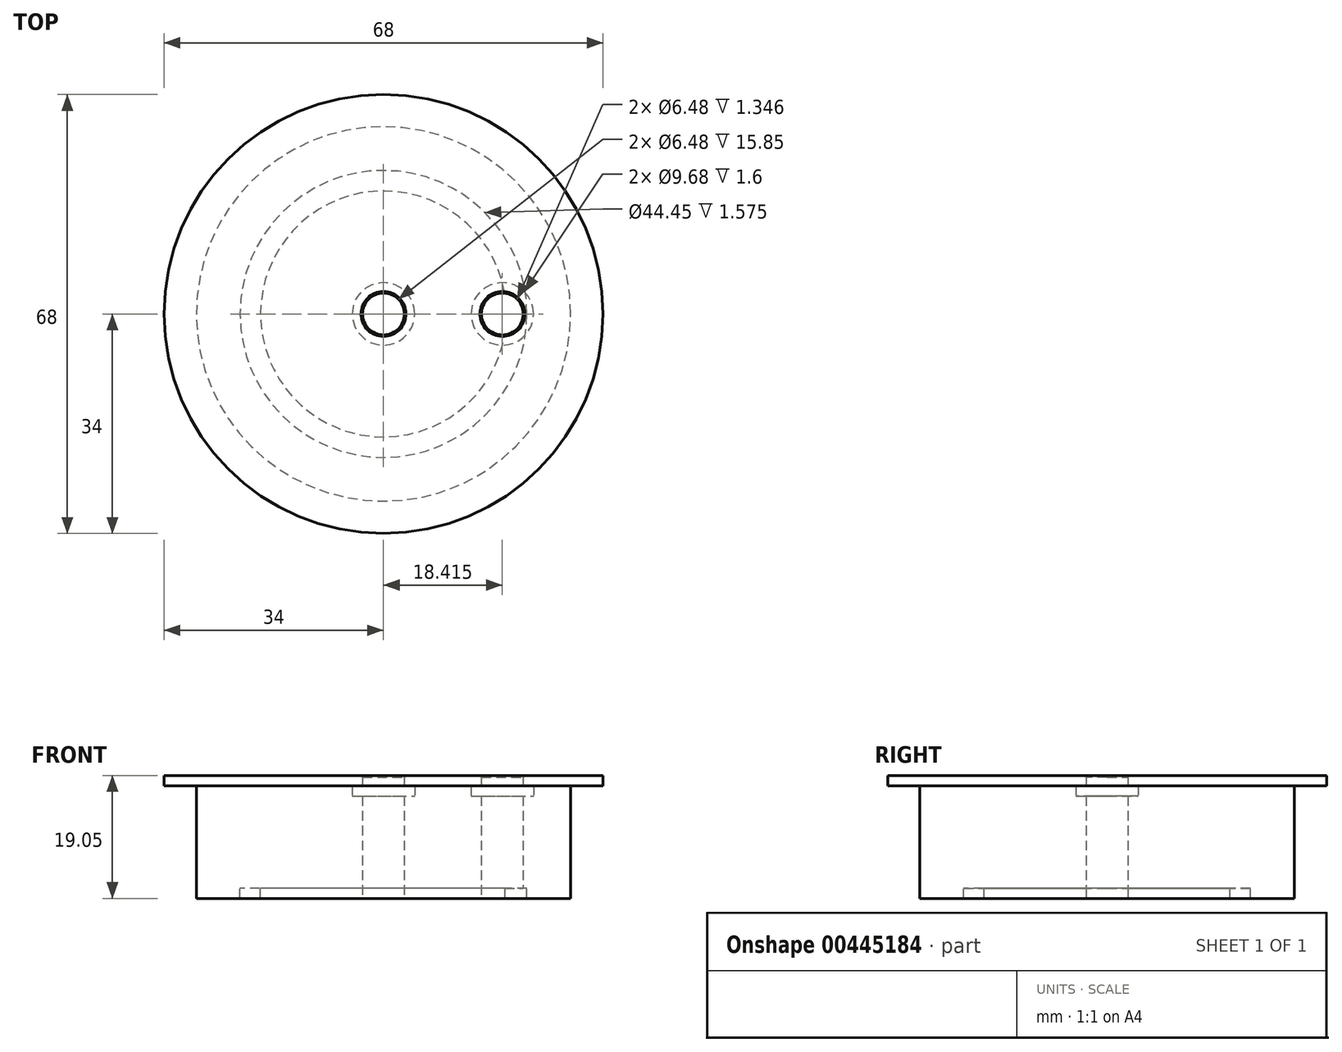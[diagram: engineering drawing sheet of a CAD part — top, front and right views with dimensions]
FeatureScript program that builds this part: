
annotation { "Feature Type Name" : "Feature", "Feature Type Description" : "" }
export const myFeature = defineFeature(function(context is Context, id is Id, definition is map)
    precondition{}
    {
        {
            var Q0;
            Q0=qCreatedBy(makeId("Front.planeOp"),FACE);
            var sketch = newSketch(context, id + "F0", { "sketchPlane" : qUnion([Q0])});
            skLineSegment(sketch, "E0", {"start": v(0, 0) * mm, "end": v(34, 0) * mm});
            skLineSegment(sketch, "E1", {"start": v(34, 0) * mm, "end": v(34, -1.6) * mm});
            skLineSegment(sketch, "E2", {"start": v(34, -1.6) * mm, "end": v(29, -1.6) * mm});
            skLineSegment(sketch, "E3", {"start": v(29, -1.6) * mm, "end": v(29, -19.05) * mm});
            skLineSegment(sketch, "E4", {"start": v(29, -19.05) * mm, "end": v(22.23, -19.05) * mm});
            skLineSegment(sketch, "E5", {"start": v(22.23, -19.05) * mm, "end": v(22.23, -17.48) * mm});
            skLineSegment(sketch, "E6", {"start": v(22.23, -17.48) * mm, "end": v(19.05, -17.48) * mm});
            skLineSegment(sketch, "E7", {"start": v(19.05, -17.48) * mm, "end": v(19.05, -19.05) * mm});
            skLineSegment(sketch, "E8", {"start": v(19.05, -19.05) * mm, "end": v(0, -19.05) * mm});
            skLineSegment(sketch, "E9", {"start": v(0, 0) * mm, "end": v(0, -19.05) * mm});
            skLineSegment(sketch, "E10", {"start": v(0, 18.94) * mm, "end": v(0, -33) * mm, "construction": true});
            skSolve(sketch);
        }
        {
            var Q0;
            Q0 = qSketchRegion(id + "F0", true);
            var Q1;
            Q1=sQuery(id+"F0.wireOp",EDGE,"E10");
            revolve(context, id + "F1", {"entities" : qUnion([Q0]), "axis" : qUnion([Q1]), "revolveType" : RevolveType.FULL});
        }
        {
            var Q0;
            Q0=makeQuery(id+"F1.opRevolve","SWEPT_FACE",FACE,{"disambiguationData":[OSD([sQuery(id+"F0.wireOp",EDGE,"E8")])]});
            var sketch = newSketch(context, id + "F2", { "sketchPlane" : qUnion([Q0])});
            skCircle(sketch, "E11", {"center": v(0, 0) * mm, "radius": 3.24 * mm});
            skCircle(sketch, "E12", {"center": v(18.41, 0) * mm, "radius": 3.24 * mm});
            skSolve(sketch);
        }
        {
            var Q0;
            Q0 = qSketchRegion(id + "F2", true);
            extrude(context, id + "F3", {"entities" : qUnion([Q0]), "operationType" : NewBodyOperationType.REMOVE, "endBound" : BoundingType.THROUGH_ALL, "oppositeDirection" : true, "depth" : 25.4 * mm});
        }
        {
            var Q0;
            Q0=qCreatedBy(makeId("Front.planeOp"),FACE);
            var sketch = newSketch(context, id + "F4", { "sketchPlane" : qUnion([Q0])});
            skLineSegment(sketch, "E13", {"start": v(0, 5.22) * mm, "end": v(0, -9.83) * mm, "construction": true});
            skLineSegment(sketch, "E14.bottom", {"start": v(3.24, -1.6) * mm, "end": v(4.84, -1.6) * mm});
            skLineSegment(sketch, "E14.top", {"start": v(3.24, -3.2) * mm, "end": v(4.84, -3.2) * mm});
            skLineSegment(sketch, "E14.left", {"start": v(3.24, -1.6) * mm, "end": v(3.24, -3.2) * mm});
            skLineSegment(sketch, "E14.right", {"start": v(4.84, -1.6) * mm, "end": v(4.84, -3.2) * mm});
            skSolve(sketch);
        }
        {
            var Q0;
            Q0 = qSketchRegion(id + "F4", true);
            var Q1;
            Q1=sQuery(id+"F4.wireOp",EDGE,"E13");
            revolve(context, id + "F5", {"operationType" : NewBodyOperationType.REMOVE, "entities" : qUnion([Q0]), "axis" : qUnion([Q1]), "revolveType" : RevolveType.FULL, "oppositeDirection" : true});
        }
        {
            var Q0;
            Q0=qCreatedBy(makeId("Front.planeOp"),FACE);
            var sketch = newSketch(context, id + "F6", { "sketchPlane" : qUnion([Q0])});
            skLineSegment(sketch, "E15", {"start": v(18.41, 2.2) * mm, "end": v(18.41, -21.08) * mm, "construction": true});
            skLineSegment(sketch, "E16.bottom", {"start": v(21.65, -1.6) * mm, "end": v(23.25, -1.6) * mm});
            skLineSegment(sketch, "E16.top", {"start": v(21.65, -3.2) * mm, "end": v(23.25, -3.2) * mm});
            skLineSegment(sketch, "E16.left", {"start": v(21.65, -1.6) * mm, "end": v(21.65, -3.2) * mm});
            skLineSegment(sketch, "E16.right", {"start": v(23.25, -1.6) * mm, "end": v(23.25, -3.2) * mm});
            skSolve(sketch);
        }
        {
            var Q0;
            Q0 = qSketchRegion(id + "F6", true);
            var Q1;
            Q1=sQuery(id+"F6.wireOp",EDGE,"E15");
            revolve(context, id + "F7", {"operationType" : NewBodyOperationType.REMOVE, "entities" : qUnion([Q0]), "axis" : qUnion([Q1]), "revolveType" : RevolveType.FULL, "oppositeDirection" : true});
        }
        {
            var Q0;
            Q0=makeQuery(id+"F3.boolean.opBoolean","INTERSECT",EDGE,{"derivedFrom":[makeQuery(id+"F1.opRevolve","SWEPT_FACE",FACE,{"disambiguationData":[OSD([sQuery(id+"F0.wireOp",EDGE,"E0")])]}),makeQuery(id+"F3.opExtrude","SWEPT_FACE",FACE,{"disambiguationData":[OSD([sQuery(id+"F2.wireOp",EDGE,"E11")])]})]});
            var Q1;
            Q1=makeQuery(id+"F3.boolean.opBoolean","INTERSECT",EDGE,{"derivedFrom":[makeQuery(id+"F1.opRevolve","SWEPT_FACE",FACE,{"disambiguationData":[OSD([sQuery(id+"F0.wireOp",EDGE,"E0")])]}),makeQuery(id+"F3.opExtrude","SWEPT_FACE",FACE,{"disambiguationData":[OSD([sQuery(id+"F2.wireOp",EDGE,"E12")])]})]});
            chamfer(context, id + "F8", {"entities" : qUnion([Q0, Q1]), "width" : 0.25 * mm, "tangentPropagation" : true});
        }
    });
